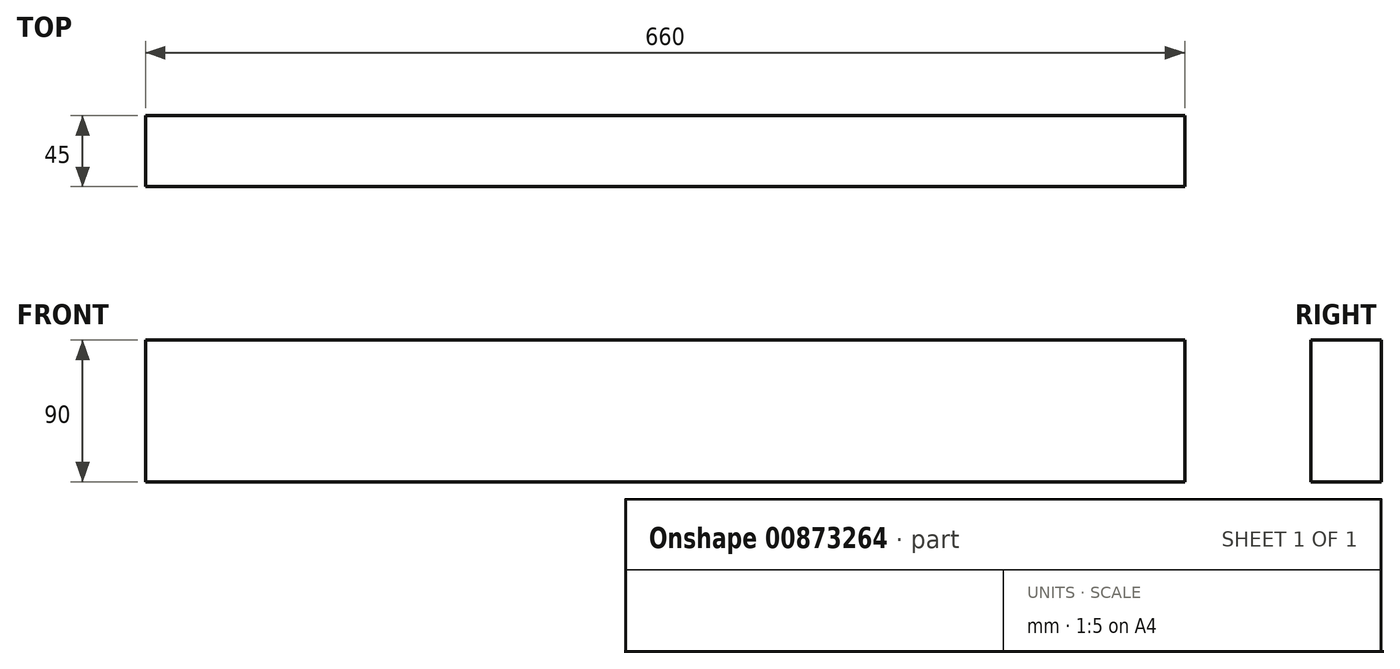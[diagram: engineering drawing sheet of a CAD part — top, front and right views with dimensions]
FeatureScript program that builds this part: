
annotation { "Feature Type Name" : "Feature", "Feature Type Description" : "" }
export const myFeature = defineFeature(function(context is Context, id is Id, definition is map)
    precondition{}
    {
        {
            var Q0;
            Q0=qCreatedBy(makeId("Front.planeOp"),FACE);
            var sketch = newSketch(context, id + "F0", { "sketchPlane" : qUnion([Q0])});
            skLineSegment(sketch, "E0.bottom", {"start": v(-330, 45) * mm, "end": v(330, 45) * mm});
            skLineSegment(sketch, "E0.top", {"start": v(-330, -45) * mm, "end": v(330, -45) * mm});
            skLineSegment(sketch, "E0.left", {"start": v(-330, 45) * mm, "end": v(-330, -45) * mm});
            skLineSegment(sketch, "E0.right", {"start": v(330, 45) * mm, "end": v(330, -45) * mm});
            skPoint(sketch, "E0.middle", {"position": v(0, 0) * mm});
            skSolve(sketch);
        }
        {
            var Q0;
            Q0=makeQuery(id+"F0.imprint","IMPRINT",FACE,{"disambiguationData":[TD([[makeQuery(id+"F0.imprint","IMPRINT",EDGE,{"derivedFrom":sQuery(id+"F0.wireOp",EDGE,"E0.bottom")}),-1.0]])]});
            extrude(context, id + "F1", {"entities" : qUnion([Q0]), "depth" : 45 * mm, "offsetDistance" : 25 * mm});
        }
    });
